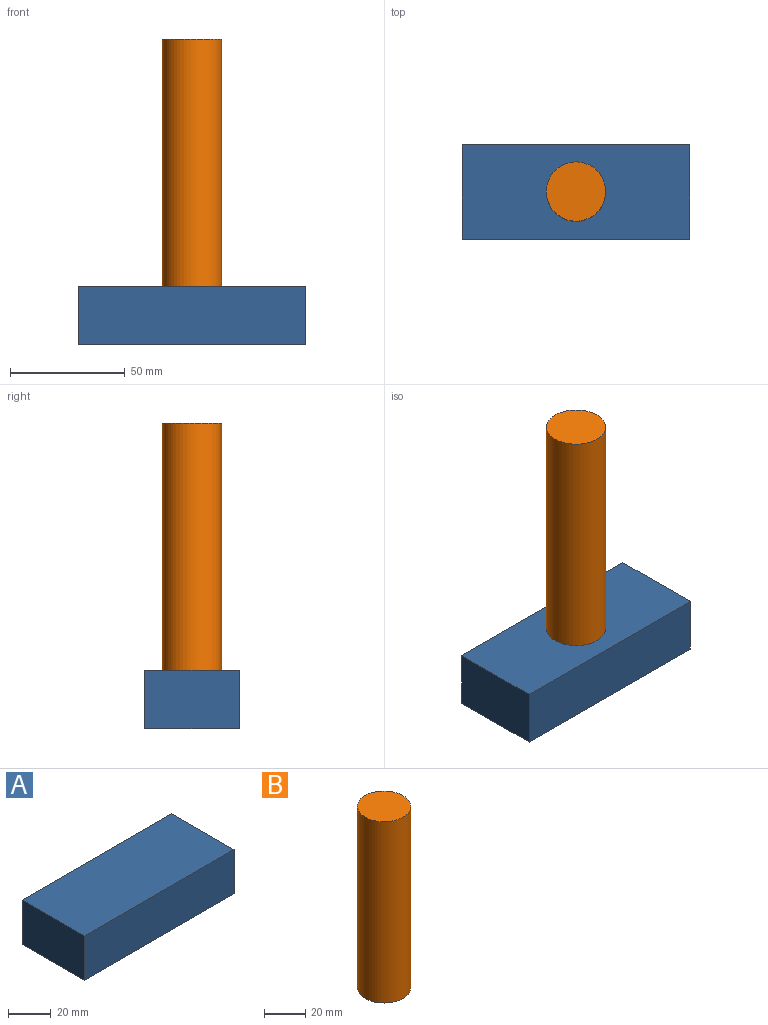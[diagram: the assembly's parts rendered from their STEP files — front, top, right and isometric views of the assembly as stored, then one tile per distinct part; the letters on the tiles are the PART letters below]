
ASSEMBLY  parts=2 mates=1
PART A: 6 faces, bbox 99.2x41.3x25.4 mm
  f0: plane 99.19x25.4mm, normal (0,1,0), area 2519.4mm2, adj f1,f3,f4,f5
  f1: plane 41.32x25.4mm, normal (-1,0,0), area 1049.4mm2, adj f0,f2,f4,f5
  f2: plane 99.19x25.4mm, normal (0,-1,0), area 2519.4mm2, adj f1,f3,f4,f5
  f3: plane 41.32x25.4mm, normal (1,0,0), area 1049.4mm2, adj f0,f2,f4,f5
  f4: plane 99.19x41.32mm, normal (0,0,1), area 4098mm2, adj f0,f1,f2,f3
  f5: plane 99.19x41.32mm, normal (0,0,-1), area 4098mm2, adj f0,f1,f2,f3
PART B: 3 faces, bbox 25.8x25.8x107.4 mm
  f0: cylinder r=12.9mm len=107.44mm, axis (0,0,-1), area 8711mm2, adj f1,f2
  f1: plane 25.81x25.81mm, normal (0,0,1), area 523.1mm2, adj f0
  f2: plane 25.81x25.81mm, normal (0,0,-1), area 523.1mm2, adj f0
PLACE A t=(-24.24,15.08,-21.23)mm
PLACE B rot(axis=(1,0,0),180deg) t=(-24.97,35.74,111.61)mm
MATE fastened B.f0 <-> A.f4  axis (0,0,-1) through (-24.97,35.74,4.17)mm
